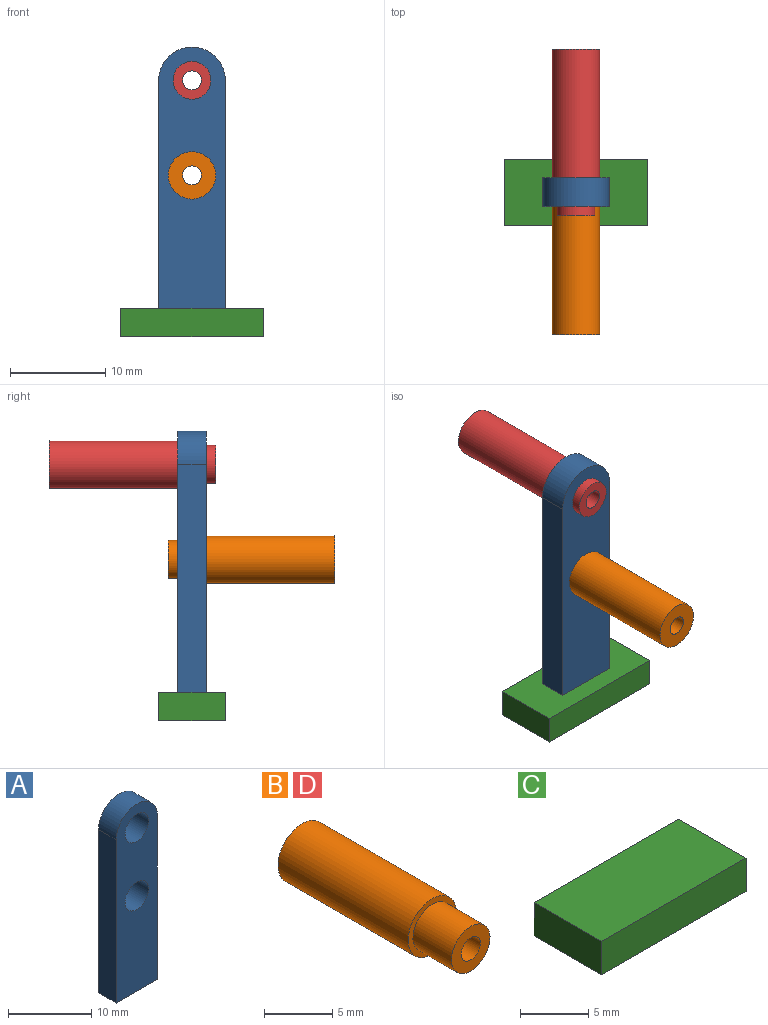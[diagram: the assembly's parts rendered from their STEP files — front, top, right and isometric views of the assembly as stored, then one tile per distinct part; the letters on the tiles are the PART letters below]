
ASSEMBLY  parts=4 mates=3
PART A: 8 faces, bbox 7x3x27.5 mm
  f0: plane 24x3mm, normal (1,0,0), area 72mm2, adj f1,f3,f4,f5
  f1: cylinder r=3.5mm len=7mm, axis (0,1,0), area 33mm2, adj f0,f2,f4,f5
  f2: plane 24x3mm, normal (-1,0,0), area 72mm2, adj f1,f3,f4,f5
  f3: plane 7x3mm, normal (0,0,-1), area 21mm2, adj f0,f2,f4,f5
  f4: plane 27.5x7mm, normal (0,-1,0), area 162.1mm2, adj f0,f1,f2,f3,f6,f7
  f5: plane 27.5x7mm, normal (0,1,0), area 162.1mm2, adj f0,f1,f2,f3,f6,f7
  f6: cylinder r=2mm len=4mm, axis (0,-1,0), area 37.7mm2, adj f4,f5
  f7: cylinder r=2mm len=4mm, axis (0,-1,0), area 37.7mm2, adj f4,f5
PART B: 6 faces, bbox 5x17.5x5 mm
  f0: cylinder r=2.5mm len=13.5mm, axis (0,1,0), area 212.1mm2, adj f1,f2
  f1: plane 5x5mm, normal (0,-1,0), area 7.1mm2, adj f0,f3
  f2: plane 5x5mm, normal (0,1,0), area 16.5mm2, adj f0,f5
  f3: cylinder r=2mm len=4mm, axis (0,1,0), area 50.3mm2, adj f1,f4
  f4: plane 4x4mm, normal (0,-1,0), area 9.4mm2, adj f3,f5
  f5: cylinder r=1mm len=17.5mm, axis (0,-1,0), area 110mm2, adj f2,f4
PART C: 6 faces, bbox 15x7x3 mm
  f0: plane 7x3mm, normal (-1,0,0), area 21mm2, adj f1,f3,f4,f5
  f1: plane 15x3mm, normal (0,-1,0), area 45mm2, adj f0,f2,f4,f5
  f2: plane 7x3mm, normal (1,0,0), area 21mm2, adj f1,f3,f4,f5
  f3: plane 15x3mm, normal (0,1,0), area 45mm2, adj f0,f2,f4,f5
  f4: plane 15x7mm, normal (0,0,1), area 105mm2, adj f0,f1,f2,f3
  f5: plane 15x7mm, normal (0,0,-1), area 105mm2, adj f0,f1,f2,f3
PART D: same geometry as B
PLACE A t=(0.71,-3.34,-6.37)mm
PLACE B rot(axis=(0,0,1),180deg) t=(0.71,-19.84,7.63)mm
PLACE C t=(-6.79,-8.34,-9.37)mm
PLACE D t=(0.71,10.16,17.63)mm
MATE fastened A.f3 <-> C.f4  axis (0,0,-1) through (0.71,-4.84,-6.37)mm
MATE fastened D.f3 <-> A.f1  axis (0,1,0) through (0.71,-3.34,17.63)mm
MATE fastened A.f6 <-> B.f3  axis (0,-1,0) through (0.71,-6.34,7.63)mm
